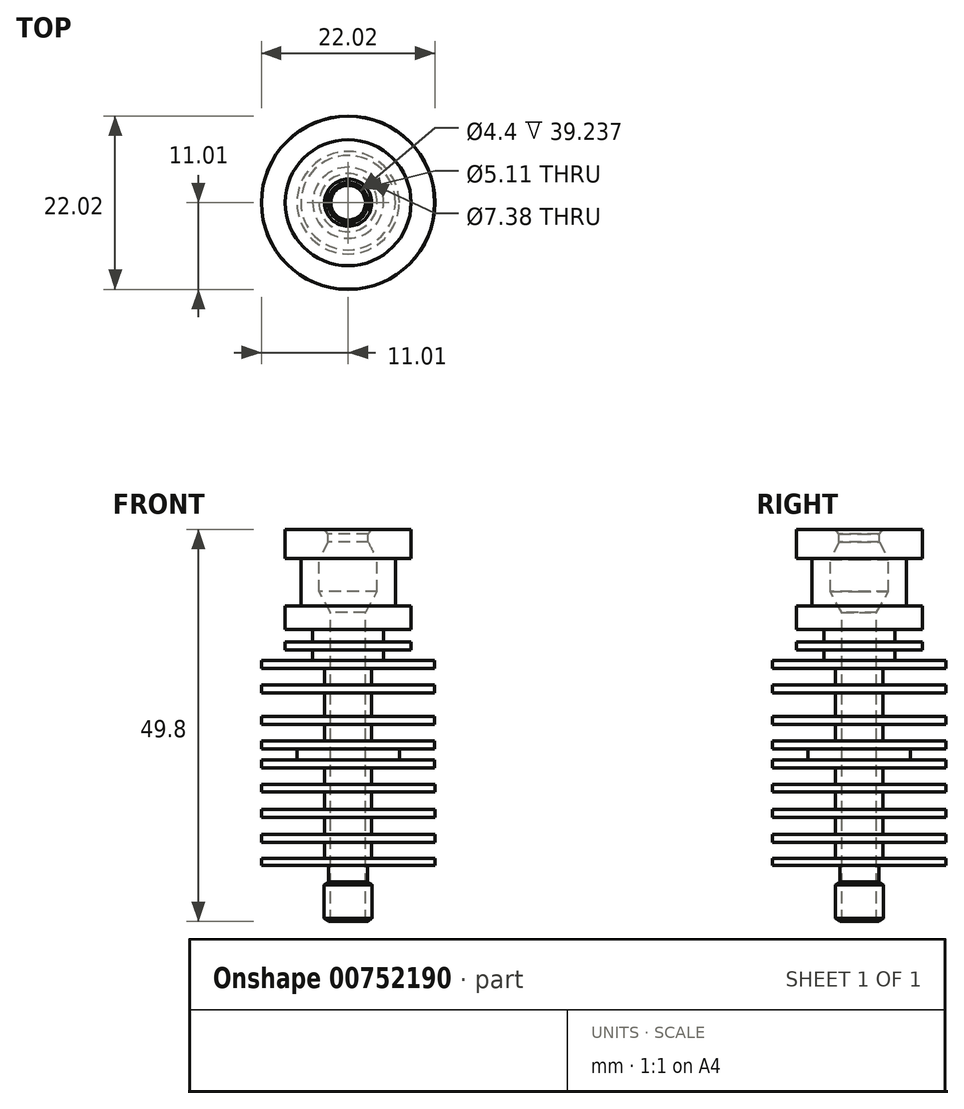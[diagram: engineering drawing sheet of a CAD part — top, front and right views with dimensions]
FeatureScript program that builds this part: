
annotation { "Feature Type Name" : "Feature", "Feature Type Description" : "" }
export const myFeature = defineFeature(function(context is Context, id is Id, definition is map)
    precondition{}
    {
        {
            var Q0;
            Q0=qCreatedBy(makeId("Front.planeOp"),FACE);
            var sketch = newSketch(context, id + "F0", { "sketchPlane" : qUnion([Q0])});
            skLineSegment(sketch, "E0", {"start": v(0, 61.45) * mm, "end": v(0, -25.18) * mm, "construction": true});
            skPoint(sketch, "E1", {"position": v(0, 49.8) * mm});
            skPoint(sketch, "E2", {"position": v(0, 7.1) * mm});
            skLineSegment(sketch, "E3", {"start": v(0, 49.8) * mm, "end": v(8, 49.8) * mm});
            skLineSegment(sketch, "E4", {"start": v(8, 49.8) * mm, "end": v(8, 46.1) * mm});
            skLineSegment(sketch, "E5", {"start": v(8, 46.1) * mm, "end": v(6, 46.1) * mm});
            skLineSegment(sketch, "E6", {"start": v(6, 46.1) * mm, "end": v(6, 40.1) * mm});
            skLineSegment(sketch, "E7", {"start": v(6, 40.1) * mm, "end": v(8, 40.1) * mm});
            skLineSegment(sketch, "E8", {"start": v(8, 40.1) * mm, "end": v(8, 37.1) * mm});
            skLineSegment(sketch, "E9", {"start": v(8, 37.1) * mm, "end": v(4.5, 37.1) * mm});
            skLineSegment(sketch, "E10", {"start": v(4.5, 37.1) * mm, "end": v(4.5, 35.52) * mm});
            skLineSegment(sketch, "E11", {"start": v(4.5, 35.52) * mm, "end": v(8, 35.52) * mm});
            skLineSegment(sketch, "E12", {"start": v(8, 35.52) * mm, "end": v(8, 34.52) * mm});
            skLineSegment(sketch, "E13", {"start": v(8, 34.52) * mm, "end": v(4.5, 34.52) * mm});
            skLineSegment(sketch, "E14", {"start": v(4.5, 34.52) * mm, "end": v(4.5, 33.13) * mm});
            skLineSegment(sketch, "E15", {"start": v(4.5, 33.13) * mm, "end": v(11, 33.13) * mm});
            skLineSegment(sketch, "E16", {"start": v(11, 33.13) * mm, "end": v(11, 32.13) * mm});
            skLineSegment(sketch, "E17", {"start": v(11, 32.13) * mm, "end": v(3, 32.13) * mm});
            skLineSegment(sketch, "E18", {"start": v(3, 32.13) * mm, "end": v(3, 30.03) * mm});
            skLineSegment(sketch, "E19", {"start": v(3, 30.03) * mm, "end": v(11, 30.03) * mm});
            skLineSegment(sketch, "E20", {"start": v(11, 30.03) * mm, "end": v(11, 29.03) * mm});
            skLineSegment(sketch, "E21", {"start": v(11, 29.03) * mm, "end": v(3, 29.03) * mm});
            skLineSegment(sketch, "E22", {"start": v(3, 29.03) * mm, "end": v(3, 26.03) * mm});
            skLineSegment(sketch, "E23", {"start": v(3, 26.03) * mm, "end": v(11, 26.03) * mm});
            skLineSegment(sketch, "E24", {"start": v(11, 26.03) * mm, "end": v(11, 25.03) * mm});
            skLineSegment(sketch, "E25", {"start": v(11, 25.03) * mm, "end": v(3, 25.03) * mm});
            skLineSegment(sketch, "E26", {"start": v(3, 25.03) * mm, "end": v(3, 22.93) * mm});
            skLineSegment(sketch, "E27", {"start": v(3, 22.93) * mm, "end": v(11, 22.93) * mm});
            skLineSegment(sketch, "E28", {"start": v(11, 22.93) * mm, "end": v(11, 21.93) * mm});
            skLineSegment(sketch, "E29", {"start": v(11, 21.93) * mm, "end": v(6.5, 21.93) * mm});
            skLineSegment(sketch, "E30", {"start": v(6.5, 21.93) * mm, "end": v(6.5, 20.53) * mm});
            skLineSegment(sketch, "E31", {"start": v(6.5, 20.53) * mm, "end": v(11, 20.53) * mm});
            skLineSegment(sketch, "E32", {"start": v(11, 20.53) * mm, "end": v(11, 19.53) * mm});
            skLineSegment(sketch, "E33", {"start": v(11, 19.53) * mm, "end": v(3, 19.53) * mm});
            skLineSegment(sketch, "E34", {"start": v(3, 19.53) * mm, "end": v(3, 17.43) * mm});
            skLineSegment(sketch, "E35", {"start": v(3, 17.43) * mm, "end": v(11.01, 17.43) * mm});
            skLineSegment(sketch, "E36", {"start": v(11.01, 17.43) * mm, "end": v(11.01, 16.43) * mm});
            skLineSegment(sketch, "E37", {"start": v(11.01, 16.43) * mm, "end": v(3, 16.43) * mm});
            skLineSegment(sketch, "E38", {"start": v(3, 16.43) * mm, "end": v(3, 14.23) * mm});
            skLineSegment(sketch, "E39", {"start": v(3, 14.23) * mm, "end": v(11.01, 14.23) * mm});
            skLineSegment(sketch, "E40", {"start": v(11.01, 14.23) * mm, "end": v(11.01, 13.23) * mm});
            skLineSegment(sketch, "E41", {"start": v(11.01, 13.23) * mm, "end": v(3, 13.23) * mm});
            skLineSegment(sketch, "E42", {"start": v(3, 13.23) * mm, "end": v(3, 11.03) * mm});
            skLineSegment(sketch, "E43", {"start": v(3, 11.03) * mm, "end": v(11.01, 11.03) * mm});
            skLineSegment(sketch, "E44", {"start": v(11.01, 11.03) * mm, "end": v(11.01, 10.03) * mm});
            skLineSegment(sketch, "E45", {"start": v(11.01, 10.03) * mm, "end": v(3, 10.03) * mm});
            skLineSegment(sketch, "E46", {"start": v(3, 10.03) * mm, "end": v(3, 8.03) * mm});
            skLineSegment(sketch, "E47", {"start": v(3, 8.03) * mm, "end": v(11.01, 8.03) * mm});
            skLineSegment(sketch, "E48", {"start": v(11.01, 8.03) * mm, "end": v(11.01, 7.1) * mm});
            skLineSegment(sketch, "E49", {"start": v(2.48, 7.1) * mm, "end": v(11.01, 7.1) * mm});
            skLineSegment(sketch, "E50", {"start": v(0, 49.8) * mm, "end": v(0, 7.1) * mm});
            skPoint(sketch, "E51", {"position": v(2.2, 7.1) * mm});
            skLineSegment(sketch, "E52", {"start": v(2.2, 7.1) * mm, "end": v(2.2, 0) * mm});
            skLineSegment(sketch, "E53", {"start": v(2.2, 7.1) * mm, "end": v(2.2, 39.24) * mm});
            skLineSegment(sketch, "E54", {"start": v(2.2, 39.24) * mm, "end": v(3.69, 41.9) * mm});
            skLineSegment(sketch, "E55", {"start": v(3.69, 41.9) * mm, "end": v(3.69, 45.97) * mm});
            skLineSegment(sketch, "E56", {"start": v(3.69, 45.97) * mm, "end": v(2.56, 48.21) * mm});
            skLineSegment(sketch, "E57", {"start": v(2.56, 48.21) * mm, "end": v(2.56, 49.21) * mm});
            skLineSegment(sketch, "E58", {"start": v(2.56, 49.21) * mm, "end": v(3, 49.8) * mm});
            skLineSegment(sketch, "E59", {"start": v(2.48, 7.1) * mm, "end": v(2.48, 5) * mm});
            skLineSegment(sketch, "E60", {"start": v(2.48, 5) * mm, "end": v(3.05, 4.67) * mm});
            skLineSegment(sketch, "E61", {"start": v(3.05, 4.67) * mm, "end": v(3.05, 0.4) * mm});
            skLineSegment(sketch, "E62", {"start": v(3.05, 0.4) * mm, "end": v(2.48, 0) * mm});
            skLineSegment(sketch, "E63", {"start": v(2.48, 0) * mm, "end": v(2.2, 0) * mm});
            skPoint(sketch, "E64", {"position": v(0, 0) * mm});
            skSolve(sketch);
        }
        {
            var Q0;
            {var subQ1=sQuery(id+"F0.wireOp",EDGE,"E4");Q0=makeQuery(id+"F0.imprint","IMPRINT",FACE,{"disambiguationData":[TD([[makeQuery(id+"F0.imprint","IMPRINT",EDGE,{"derivedFrom":subQ1}),-1.0]])]});}
            var Q1;
            Q1=sQuery(id+"F0.wireOp",EDGE,"E0");
            revolve(context, id + "F1", {"surfaceOperationType" : NewSurfaceOperationType.NEW, "entities" : qUnion([Q0]), "axis" : qUnion([Q1]), "revolveType" : RevolveType.FULL});
        }
    });
